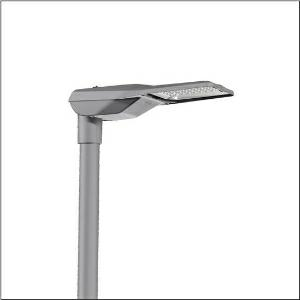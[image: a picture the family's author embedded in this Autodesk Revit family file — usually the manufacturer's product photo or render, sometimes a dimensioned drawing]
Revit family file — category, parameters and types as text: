
# Revit family: streetlight_sl_21_mini___stw1_0a_5xe2e43s08gb_9e9f
name_source: partatom
category: Lighting Fixtures
units: mm (PartAtom-declared; Revit-internal decimal feet)

## family parameters
Cut with Voids When Loaded = No
Host = Face
Light Source = No
Part Type = Normal
Room Calculation Point = No
Round Connector Dimension = Use Diameter
Shared = No

## types (1)
- --- (1 x LED, 6180 lm, 40.4 W, 4000K)
    Apparent Load = 40 VA
    CIE Flux Codes = 38 75 98 100 100
    Color Rendering = 70
    Color Temperature = 4000K
    Default Elevation = 1800 mm
    Description = Streetlight SL 21 mini, mast luminaire, primary light control with lens, of PMMA, primary optical cover: cover, of toughened safety glass, transparent, light distribution: STW1.0a, light emission: direct distribution, primary light characteristic: asymmetric, installation type: side-entry, post-top, LED, High Power LED, rated luminous flux: 6.180lm, luminous efficacy: 153lm/W, light colour: 740, colour temperature: 4000K, control gear: D4i, control: overheat protection, constant luminous flux control, time-dependent luminous flux control, flexible luminous flux parameterisation, pre-setting: logarithmic dimming characteristic, mains connection: 220..240V, AC, 50/60Hz, start of lifetime: 40W, end of service life: 41W, reduction: 19W, luminaire housing, of diecast aluminium, powder-coated, SITECO metallic grey (DB 702S), corrosivity category C5 high according to DIN EN ISO 12944, please order mast flange separately, inclination adjustable: 0°, 5°, 10°, 15°, sealing non-destructively replaceable, multi-level sealing system, length: 628mm, width: 235mm, height: 110mm, mast flange for spigot size: 42mm (side-entry): 5XC10008XM4, 60/48mm (side-entry/post-top): 5XC10108XM2, 76/60mm (side-entry/post-top): 5XC10108XM1, mounting height: 4..8m, Smart Interface above, protection rating (complete): IP66, insulation class (complete): insulation class II (safety insulation), certification: CE, ENEC, ENEC+, VDE, impact resistance: IK10, permissible operating ambient temperature for outdoor applications: -40..+50°C, standard-compliant lighting for roads and squares, packaging unit: 1 piece

Light Distribution: STW1.0a
    Height = 110 mm
    Lamp = 1 x LED
    Lamp Light Flux = 6180 lm
    Lamp Power = 40.4 W
    Lamp count = 1
    Length = 625 mm
    Luminous efficacy = 153 lm/W
    Manufacturer = Siteco
    ModVariant = No
    Model = 5XE2E43S08GB
    Number of Poles = 1
    OnlyDefault = Yes
    Power Factor = 1
    Product Name = Streetlight SL 21 mini | STW1.0a
    Product group = mast luminaire | pylon top
    ProductGroupID = 6100
    Protection Class = Protection class II
    Protection Degree = IP 66
    RLX_Detail_Level = 1
    RLX_Emergency_Light_Flux = 0 lm
    RLX_Emergency_Type = 0
    RLX_Emergency_Type_DB = No
    RlxData = <blob elided: 26217 chars, md5=9b9f0508>
    Socket = socket
    Standby Power = 0 W
    System Light Flux = 6180 lm
    System Power = 40 W
    Type Comments = factory setting: luminous flux: 100 % | dim-lin: 254 | 812 mA
    Type Image = l_1003515.jpg
    URL = http://relux.com
    VarID = @adj_184871
    Voltage = 0 V
    Weight = 0.00 kg
    Width = 234 mm

## geometry (parser evidence)
native form markers: Blend x4, Sweep x10
no freeform markers — native parametric forms only
